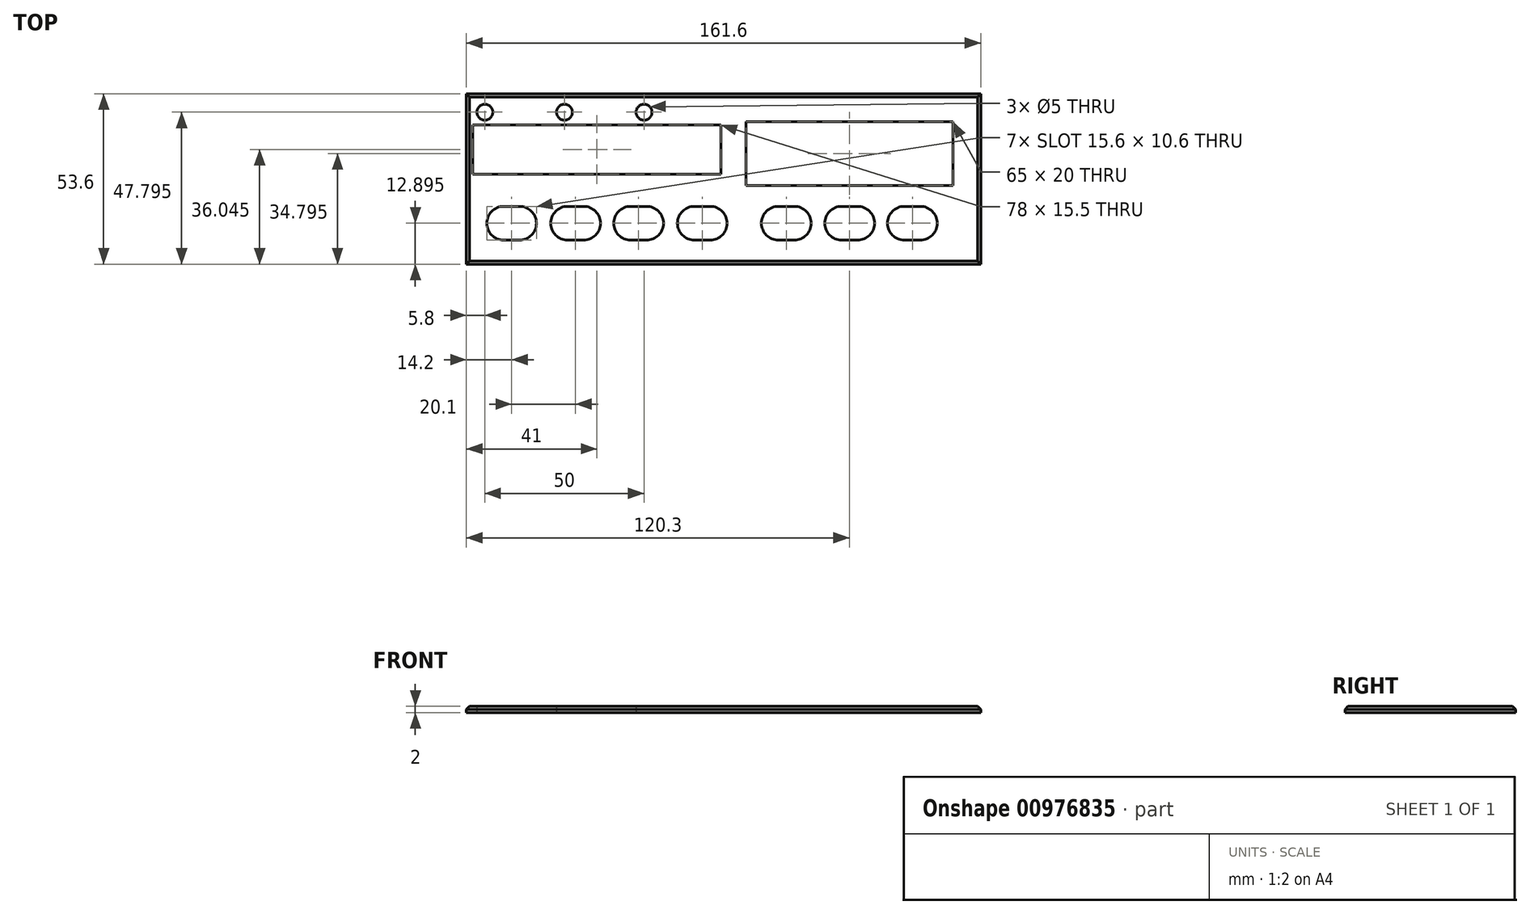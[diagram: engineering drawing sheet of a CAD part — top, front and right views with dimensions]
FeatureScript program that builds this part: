
annotation { "Feature Type Name" : "Feature", "Feature Type Description" : "" }
export const myFeature = defineFeature(function(context is Context, id is Id, definition is map)
    precondition{}
    {
        {
            var Q0;
            Q0=qCreatedBy(makeId("Top.planeOp"),FACE);
            var sketch = newSketch(context, id + "F0", { "sketchPlane" : qUnion([Q0])});
            skLineSegment(sketch, "E0.bottom", {"start": v(-80.8, -54.5) * mm, "end": v(80.8, -54.5) * mm});
            skLineSegment(sketch, "E0.top", {"start": v(-80.8, -108.1) * mm, "end": v(80.8, -108.1) * mm});
            skLineSegment(sketch, "E0.left", {"start": v(-80.8, -54.5) * mm, "end": v(-80.8, -108.1) * mm});
            skLineSegment(sketch, "E0.right", {"start": v(80.8, -54.5) * mm, "end": v(80.8, -108.1) * mm});
            skPoint(sketch, "E0.middle", {"position": v(0, -81.3) * mm});
            skPoint(sketch, "E1", {"position": v(-75, -60.3) * mm});
            skPoint(sketch, "E2", {"position": v(-50, -60.3) * mm});
            skPoint(sketch, "E3", {"position": v(-25, -60.3) * mm});
            skLineSegment(sketch, "E4.bottom", {"start": v(-78.8, -64.3) * mm, "end": v(-0.8, -64.3) * mm});
            skLineSegment(sketch, "E4.top", {"start": v(-78.8, -79.8) * mm, "end": v(-0.8, -79.8) * mm});
            skLineSegment(sketch, "E4.left", {"start": v(-78.8, -64.3) * mm, "end": v(-78.8, -79.8) * mm});
            skLineSegment(sketch, "E4.right", {"start": v(-0.8, -64.3) * mm, "end": v(-0.8, -79.8) * mm});
            skLineSegment(sketch, "E5.bottom", {"start": v(7, -63.3) * mm, "end": v(72, -63.3) * mm});
            skLineSegment(sketch, "E5.top", {"start": v(7, -83.3) * mm, "end": v(72, -83.3) * mm});
            skLineSegment(sketch, "E5.left", {"start": v(7, -63.3) * mm, "end": v(7, -83.3) * mm});
            skLineSegment(sketch, "E5.right", {"start": v(72, -63.3) * mm, "end": v(72, -83.3) * mm});
            skPoint(sketch, "E6", {"position": v(-69.1, -95.2) * mm});
            skPoint(sketch, "E7", {"position": v(-64.1, -95.2) * mm});
            skArc(sketch, "E8", {"start": v(-69.1, -89.9) * mm, "mid": v(-74.4, -95.2) * mm, "end": v(-69.1, -100.5) * mm});
            skArc(sketch, "E9", {"start": v(-64.1, -100.5) * mm, "mid": v(-58.8, -95.2) * mm, "end": v(-64.1, -89.9) * mm});
            skLineSegment(sketch, "E10", {"start": v(-69.1, -89.9) * mm, "end": v(-64.1, -89.9) * mm});
            skLineSegment(sketch, "E11", {"start": v(-69.1, -100.5) * mm, "end": v(-64.1, -100.5) * mm});
            skPoint(sketch, "E12", {"position": v(-49, -95.2) * mm});
            skPoint(sketch, "E13", {"position": v(-44, -95.2) * mm});
            skPoint(sketch, "E14", {"position": v(-29.2, -95.2) * mm});
            skPoint(sketch, "E15", {"position": v(-24.2, -95.2) * mm});
            skPoint(sketch, "E16", {"position": v(-9.2, -95.2) * mm});
            skPoint(sketch, "E17", {"position": v(-4.2, -95.2) * mm});
            skPoint(sketch, "E18", {"position": v(17.2, -95.2) * mm});
            skPoint(sketch, "E19", {"position": v(22.2, -95.2) * mm});
            skPoint(sketch, "E20", {"position": v(37.1, -95.2) * mm});
            skPoint(sketch, "E21", {"position": v(42.1, -95.2) * mm});
            skPoint(sketch, "E22", {"position": v(56.8, -95.2) * mm});
            skPoint(sketch, "E23", {"position": v(61.8, -95.2) * mm});
            skArc(sketch, "E24", {"start": v(-49, -89.9) * mm, "mid": v(-54.3, -95.2) * mm, "end": v(-49, -100.5) * mm});
            skArc(sketch, "E25", {"start": v(-44, -89.9) * mm, "mid": v(-38.7, -95.2) * mm, "end": v(-44, -100.5) * mm});
            skArc(sketch, "E26", {"start": v(-29.2, -89.9) * mm, "mid": v(-34.5, -95.2) * mm, "end": v(-29.2, -100.5) * mm});
            skArc(sketch, "E27", {"start": v(-24.2, -89.9) * mm, "mid": v(-18.9, -95.2) * mm, "end": v(-24.2, -100.5) * mm});
            skArc(sketch, "E28", {"start": v(-9.2, -89.9) * mm, "mid": v(-14.5, -95.2) * mm, "end": v(-9.2, -100.5) * mm});
            skArc(sketch, "E29", {"start": v(-4.2, -89.9) * mm, "mid": v(1.1, -95.2) * mm, "end": v(-4.2, -100.5) * mm});
            skArc(sketch, "E30", {"start": v(17.2, -89.9) * mm, "mid": v(11.9, -95.2) * mm, "end": v(17.2, -100.5) * mm});
            skArc(sketch, "E31", {"start": v(22.2, -89.9) * mm, "mid": v(27.5, -95.2) * mm, "end": v(22.2, -100.5) * mm});
            skArc(sketch, "E32", {"start": v(37.1, -89.9) * mm, "mid": v(31.8, -95.2) * mm, "end": v(37.1, -100.5) * mm});
            skArc(sketch, "E33", {"start": v(42.1, -89.9) * mm, "mid": v(47.4, -95.2) * mm, "end": v(42.1, -100.5) * mm});
            skArc(sketch, "E34", {"start": v(56.8, -89.9) * mm, "mid": v(51.5, -95.2) * mm, "end": v(56.8, -100.5) * mm});
            skArc(sketch, "E35", {"start": v(61.8, -89.9) * mm, "mid": v(67.1, -95.2) * mm, "end": v(61.8, -100.5) * mm});
            skLineSegment(sketch, "E36", {"start": v(61.8, -89.9) * mm, "end": v(56.8, -89.9) * mm});
            skLineSegment(sketch, "E37", {"start": v(61.8, -100.5) * mm, "end": v(56.8, -100.5) * mm});
            skLineSegment(sketch, "E38", {"start": v(42.1, -89.9) * mm, "end": v(37.1, -89.9) * mm});
            skLineSegment(sketch, "E39", {"start": v(42.1, -100.5) * mm, "end": v(37.1, -100.5) * mm});
            skLineSegment(sketch, "E40", {"start": v(22.2, -89.9) * mm, "end": v(17.2, -89.9) * mm});
            skLineSegment(sketch, "E41", {"start": v(22.2, -100.5) * mm, "end": v(17.2, -100.5) * mm});
            skLineSegment(sketch, "E42", {"start": v(-4.2, -89.9) * mm, "end": v(-9.2, -89.9) * mm});
            skLineSegment(sketch, "E43", {"start": v(-24.2, -89.9) * mm, "end": v(-29.2, -89.9) * mm});
            skLineSegment(sketch, "E44", {"start": v(-44, -89.9) * mm, "end": v(-49, -89.9) * mm});
            skLineSegment(sketch, "E45", {"start": v(-49, -100.5) * mm, "end": v(-44, -100.5) * mm});
            skLineSegment(sketch, "E46", {"start": v(-29.2, -100.5) * mm, "end": v(-24.2, -100.5) * mm});
            skLineSegment(sketch, "E47", {"start": v(-9.2, -100.5) * mm, "end": v(-4.2, -100.5) * mm});
            skSolve(sketch);
        }
        {
            var Q0;
            Q0=qSketchRegion(id+"F0",true);
            extrude(context, id + "F1", {"entities" : qUnion([Q0]), "depth" : 2 * mm, "offsetDistance" : 25 * mm});
        }
        {
            var Q0;
            Q0=sQuery(id+"F0.wireOp",VERTEX,"E1");
            var Q1;
            Q1=sQuery(id+"F0.wireOp",VERTEX,"E2");
            var Q2;
            Q2=sQuery(id+"F0.wireOp",VERTEX,"E3");
            var Q3;
            Q3=makeQuery(id+"F1.opExtrude","SWEPT_BODY",BODY,{"disambiguationData":[OSD([sQuery(id+"F0.wireOp",EDGE,"E0.bottom"),sQuery(id+"F0.wireOp",EDGE,"E0.top"),sQuery(id+"F0.wireOp",EDGE,"E0.left"),sQuery(id+"F0.wireOp",EDGE,"E0.right"),sQuery(id+"F0.wireOp",EDGE,"E4.bottom"),sQuery(id+"F0.wireOp",EDGE,"E4.top"),sQuery(id+"F0.wireOp",EDGE,"E4.left"),sQuery(id+"F0.wireOp",EDGE,"E4.right"),sQuery(id+"F0.wireOp",EDGE,"E5.bottom"),sQuery(id+"F0.wireOp",EDGE,"E5.top"),sQuery(id+"F0.wireOp",EDGE,"E5.left"),sQuery(id+"F0.wireOp",EDGE,"E5.right")])]});
            hole(context, id + "F2", {"style" : HoleStyle.SIMPLE, "endStyle" : HoleEndStyle.THROUGH, "oppositeDirection" : true, "holeDiameter" : 5 * mm, "majorDiameter" : 5 * mm, "isTappedThrough" : true, "tappedDepth" : 12 * mm, "tapClearance" : 3, "locations" : qUnion([Q0, Q1, Q2]), "scope" : qUnion([Q3])});
        }
        {
            var Q0;
            Q0=makeQuery(id+"F1.opExtrude","CAP_EDGE",EDGE,{"disambiguationData":[OSD([sQuery(id+"F0.wireOp",EDGE,"E0.left")])],"isStart":false});
            var Q1;
            Q1=makeQuery(id+"F1.opExtrude","CAP_EDGE",EDGE,{"disambiguationData":[OSD([sQuery(id+"F0.wireOp",EDGE,"E0.top")])],"isStart":false});
            var Q2;
            Q2=makeQuery(id+"F1.opExtrude","CAP_EDGE",EDGE,{"disambiguationData":[OSD([sQuery(id+"F0.wireOp",EDGE,"E0.bottom")])],"isStart":false});
            var Q3;
            Q3=makeQuery(id+"F1.opExtrude","CAP_EDGE",EDGE,{"disambiguationData":[OSD([sQuery(id+"F0.wireOp",EDGE,"E0.right")])],"isStart":false});
            chamfer(context, id + "F3", {"entities" : qUnion([Q0, Q1, Q2, Q3]), "width" : 1 * mm, "tangentPropagation" : true});
        }
    });
